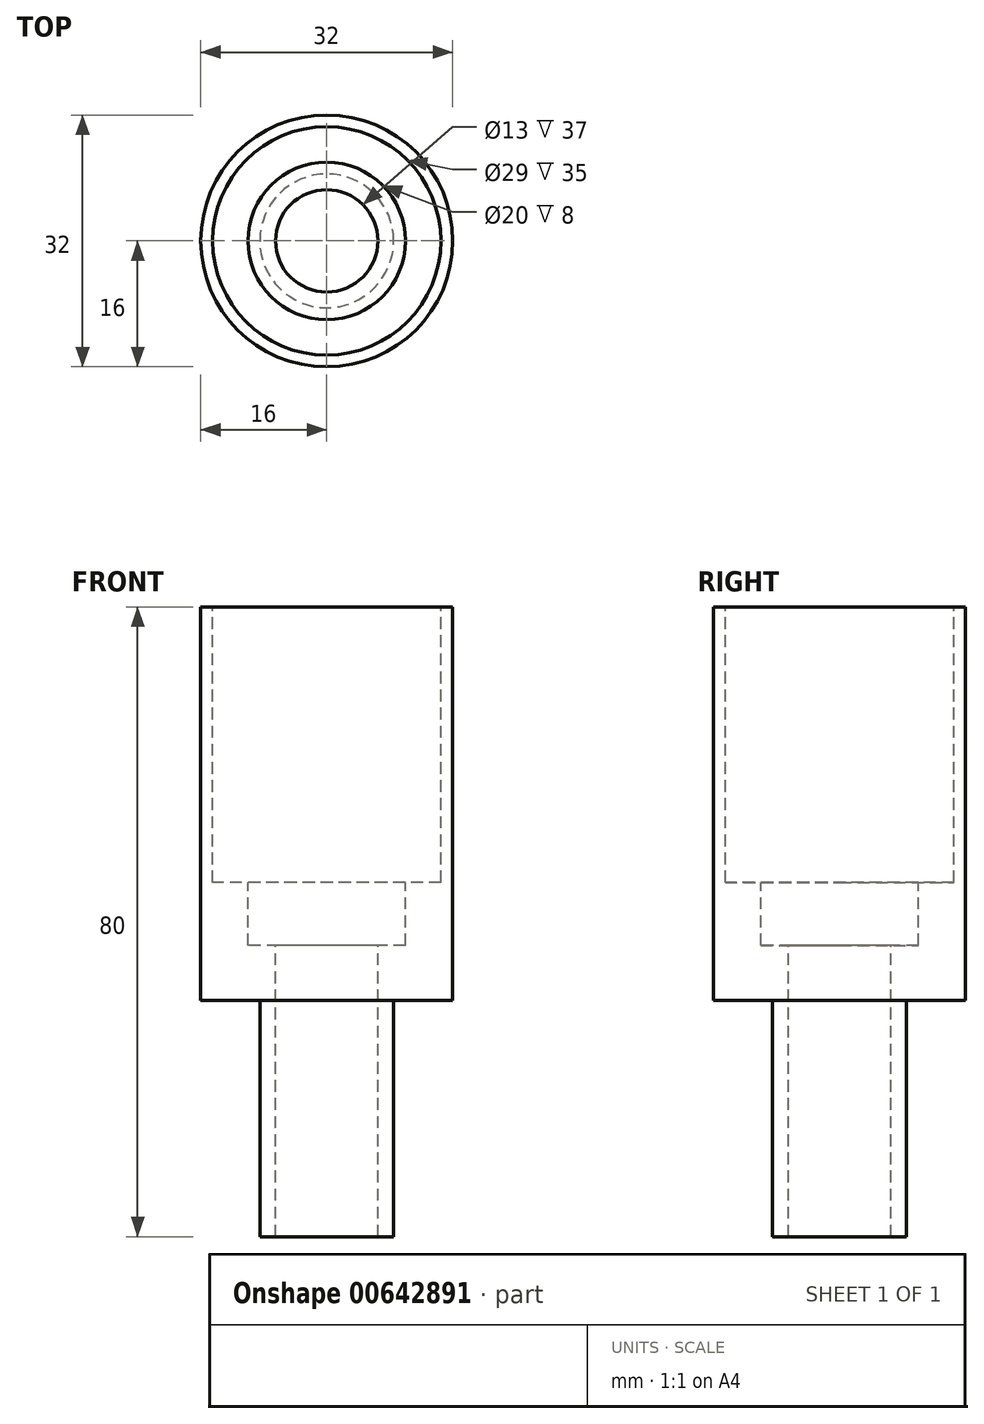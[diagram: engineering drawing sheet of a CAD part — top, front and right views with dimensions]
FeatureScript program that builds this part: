
annotation { "Feature Type Name" : "Feature", "Feature Type Description" : "" }
export const myFeature = defineFeature(function(context is Context, id is Id, definition is map)
    precondition{}
    {
        {
            var Q0;
            Q0=qCreatedBy(makeId("Top.planeOp"),FACE);
            var sketch = newSketch(context, id + "F0", { "sketchPlane" : qUnion([Q0])});
            skCircle(sketch, "E0", {"center": v(0, 0) * mm, "radius": 16 * mm});
            skSolve(sketch);
        }
        {
            var Q0;
            Q0=makeQuery(id+"F0.imprint","IMPRINT",FACE,{"disambiguationData":[TD([[makeQuery(id+"F0.imprint","IMPRINT",EDGE,{"derivedFrom":sQuery(id+"F0.wireOp",EDGE,"E0")}),1.0]])]});
            extrude(context, id + "F1", {"entities" : qUnion([Q0]), "depth" : 50 * mm, "offsetDistance" : 25.4 * mm});
        }
        {
            var Q0;
            Q0=makeQuery(id+"F1.opExtrude","CAP_FACE",FACE,{"disambiguationData":[OSD([sQuery(id+"F0.wireOp",EDGE,"E0")])],"isStart":false});
            var sketch = newSketch(context, id + "F2", { "sketchPlane" : qUnion([Q0])});
            skCircle(sketch, "E1", {"center": v(0, 0) * mm, "radius": 14.5 * mm});
            skSolve(sketch);
        }
        {
            var Q0;
            Q0=makeQuery(id+"F2.imprint","IMPRINT",FACE,{"disambiguationData":[TD([[makeQuery(id+"F2.imprint","IMPRINT",EDGE,{"derivedFrom":sQuery(id+"F2.wireOp",EDGE,"E1")}),1.0]])]});
            extrude(context, id + "F3", {"entities" : qUnion([Q0]), "operationType" : NewBodyOperationType.REMOVE, "oppositeDirection" : true, "depth" : 35 * mm, "offsetDistance" : 25.4 * mm});
        }
        {
            var Q0;
            Q0=makeQuery(id+"F1.opExtrude","CAP_FACE",FACE,{"disambiguationData":[OSD([sQuery(id+"F0.wireOp",EDGE,"E0")])],"isStart":true});
            var sketch = newSketch(context, id + "F4", { "sketchPlane" : qUnion([Q0])});
            skCircle(sketch, "E2", {"center": v(0, 0) * mm, "radius": 8.5 * mm});
            skSolve(sketch);
        }
        {
            var Q0;
            Q0 = qSketchRegion(id + "F4", true);
            var Q1;
            Q1=makeQuery(id+"F4.imprint","IMPRINT",FACE,{"disambiguationData":[TD([[makeQuery(id+"F4.imprint","IMPRINT",EDGE,{"derivedFrom":sQuery(id+"F4.wireOp",EDGE,"E2")}),1.0]])]});
            extrude(context, id + "F5", {"entities" : qUnion([Q0, Q1]), "operationType" : NewBodyOperationType.ADD, "depth" : 30 * mm, "offsetDistance" : 25.4 * mm});
        }
        {
            var Q0;
            Q0=makeQuery(id+"F3.boolean.opBoolean","COPY",FACE,{"derivedFrom":makeQuery(id+"F3.opExtrude","CAP_FACE",FACE,{"disambiguationData":[OSD([sQuery(id+"F2.wireOp",EDGE,"E1")])],"isStart":false})});
            var sketch = newSketch(context, id + "F6", { "sketchPlane" : qUnion([Q0])});
            skCircle(sketch, "E3", {"center": v(0, 0) * mm, "radius": 6.5 * mm});
            skSolve(sketch);
        }
        {
            var Q0;
            Q0=makeQuery(id+"F6.imprint","IMPRINT",FACE,{"disambiguationData":[TD([[makeQuery(id+"F6.imprint","IMPRINT",EDGE,{"derivedFrom":sQuery(id+"F6.wireOp",EDGE,"E3")}),1.0]])]});
            var Q1;
            Q1=sQuery(id+"F6.wireOp",EDGE,"E3");
            extrude(context, id + "F7", {"entities" : qUnion([Q0]), "operationType" : NewBodyOperationType.REMOVE, "surfaceEntities" : qUnion([Q1]), "endBound" : BoundingType.THROUGH_ALL, "oppositeDirection" : true, "depth" : 25.4 * mm, "offsetDistance" : 25.4 * mm});
        }
        {
            var Q0;
            Q0=makeQuery(id+"F3.boolean.opBoolean","COPY",FACE,{"derivedFrom":makeQuery(id+"F3.opExtrude","CAP_FACE",FACE,{"disambiguationData":[OSD([sQuery(id+"F2.wireOp",EDGE,"E1")])],"isStart":false})});
            var sketch = newSketch(context, id + "F8", { "sketchPlane" : qUnion([Q0])});
            skCircle(sketch, "E4", {"center": v(0, 0) * mm, "radius": 10 * mm});
            skSolve(sketch);
        }
        {
            var Q0;
            Q0=makeQuery(id+"F8.imprint","IMPRINT",FACE,{"disambiguationData":[TD([[makeQuery(id+"F8.imprint","IMPRINT",EDGE,{"derivedFrom":sQuery(id+"F8.wireOp",EDGE,"E4")}),1.0]])]});
            extrude(context, id + "F9", {"entities" : qUnion([Q0]), "operationType" : NewBodyOperationType.REMOVE, "oppositeDirection" : true, "depth" : 8 * mm, "offsetDistance" : 25.4 * mm});
        }
    });
